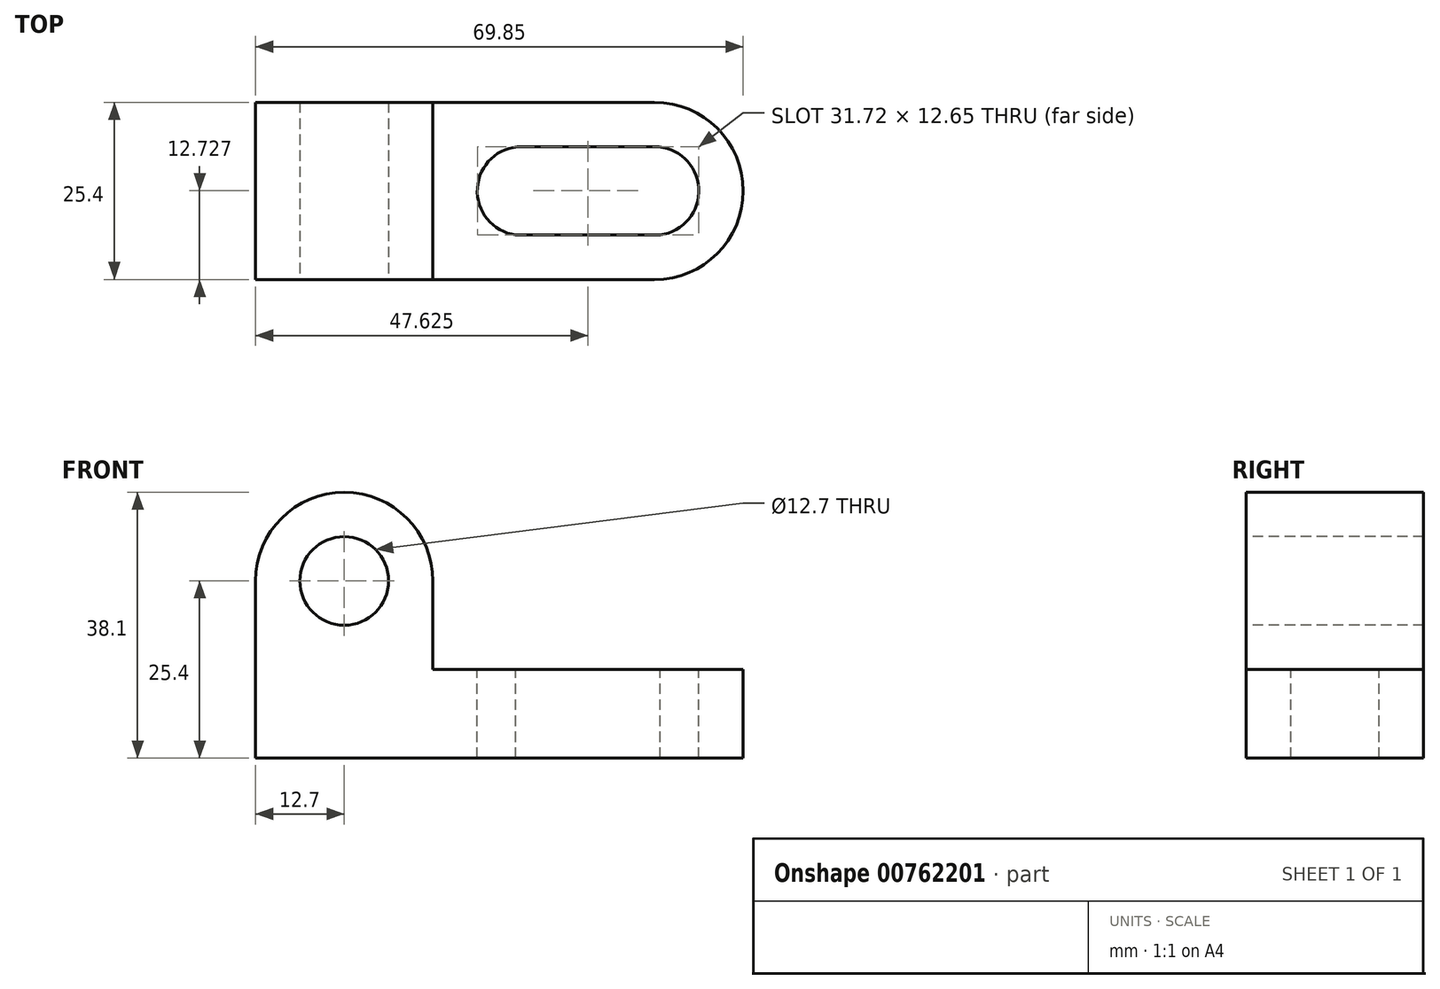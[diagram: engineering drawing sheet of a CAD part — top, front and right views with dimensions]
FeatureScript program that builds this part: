
annotation { "Feature Type Name" : "Feature", "Feature Type Description" : "" }
export const myFeature = defineFeature(function(context is Context, id is Id, definition is map)
    precondition{}
    {
        {
            var Q0;
            Q0=qCreatedBy(makeId("Front.planeOp"),FACE);
            var sketch = newSketch(context, id + "F0", { "sketchPlane" : qUnion([Q0])});
            skLineSegment(sketch, "E0", {"start": v(0, 0) * mm, "end": v(-69.85, 0) * mm});
            skLineSegment(sketch, "E1", {"start": v(-69.85, 0) * mm, "end": v(-69.85, 38.1) * mm});
            skLineSegment(sketch, "E2", {"start": v(-69.85, 38.1) * mm, "end": v(-44.45, 38.1) * mm});
            skLineSegment(sketch, "E3", {"start": v(-44.45, 38.1) * mm, "end": v(-44.45, 12.7) * mm});
            skLineSegment(sketch, "E4", {"start": v(-44.45, 12.7) * mm, "end": v(0, 12.7) * mm});
            skLineSegment(sketch, "E5", {"start": v(0, 12.7) * mm, "end": v(0, 0) * mm});
            skSolve(sketch);
        }
        {
            var Q0;
            Q0=makeQuery(id+"F0.imprint","IMPRINT",FACE,{"disambiguationData":[TD([[makeQuery(id+"F0.imprint","IMPRINT",EDGE,{"derivedFrom":sQuery(id+"F0.wireOp",EDGE,"E0")}),-1.0]])]});
            extrude(context, id + "F1", {"entities" : qUnion([Q0]), "depth" : 25.4 * mm, "offsetDistance" : 25.4 * mm});
        }
        {
            var Q0;
            Q0=makeQuery(id+"F0.imprint","IMPRINT",FACE,{"disambiguationData":[TD([[makeQuery(id+"F0.imprint","IMPRINT",EDGE,{"derivedFrom":sQuery(id+"F0.wireOp",EDGE,"E0")}),-1.0]])]});
            extrude(context, id + "F2", {"entities" : qUnion([Q0]), "operationType" : NewBodyOperationType.ADD, "depth" : 25.4 * mm, "offsetDistance" : 25.4 * mm});
        }
        {
            var Q0;
            Q0=makeQuery(id+"F1.opExtrude","SWEPT_FACE",FACE,{"disambiguationData":[OSD([sQuery(id+"F0.wireOp",EDGE,"E4")])]});
            var sketch = newSketch(context, id + "F3", { "sketchPlane" : qUnion([Q0])});
            skLineSegment(sketch, "E6", {"start": v(-38.1, 0) * mm, "end": v(-38.1, -25.4) * mm});
            skLineSegment(sketch, "E7", {"start": v(-6.35, 0) * mm, "end": v(-6.35, -25.4) * mm});
            skLineSegment(sketch, "E8", {"start": v(-38.1, -6.35) * mm, "end": v(-6.35, -6.35) * mm});
            skLineSegment(sketch, "E9", {"start": v(-38.1, -19) * mm, "end": v(-6.35, -19) * mm});
            skCircle(sketch, "E10", {"center": v(2.1, -12.84) * mm, "radius": 1.17 * mm});
            skLineSegment(sketch, "E11", {"start": v(-31.75, 0) * mm, "end": v(-31.75, -25.4) * mm});
            skLineSegment(sketch, "E12", {"start": v(-12.7, 0) * mm, "end": v(-12.7, -25.4) * mm});
            skCircle(sketch, "E13", {"center": v(-31.75, -12.7) * mm, "radius": 6.35 * mm});
            skCircle(sketch, "E14", {"center": v(-12.7, -12.7) * mm, "radius": 6.35 * mm});
            skSolve(sketch);
        }
        {
            var Q0;
            {var subQ0=sQuery(id+"F3.wireOp",EDGE,"E11");var subQ1=sQuery(id+"F3.wireOp",EDGE,"E9");var subQ2=makeQuery(id+"F3.imprint","INTERSECT",VERTEX,{"derivedFrom":[subQ1,subQ0]});Q0=makeQuery(id+"F3.imprint","IMPRINT",FACE,{"disambiguationData":[TD([[makeQuery(id+"F3.imprint","IMPRINT",EDGE,{"disambiguationData":[TD([[subQ2,-1.0]])],"derivedFrom":subQ1}),1.0]])]});}
            var Q1;
            {var subQ0=sQuery(id+"F3.wireOp",EDGE,"E13");var subQ1=sQuery(id+"F3.wireOp",EDGE,"E9");var subQ2=makeQuery(id+"F3.imprint","INTERSECT",VERTEX,{"disambiguationData":[OD(0.0)],"derivedFrom":[subQ1,subQ0]});Q1=makeQuery(id+"F3.imprint","IMPRINT",FACE,{"disambiguationData":[TD([[makeQuery(id+"F3.imprint","IMPRINT",EDGE,{"disambiguationData":[TD([[subQ2,-1.0]])],"derivedFrom":subQ1}),1.0]])]});}
            var Q2;
            {var subQ0=sQuery(id+"F3.wireOp",EDGE,"E14");var subQ1=sQuery(id+"F3.wireOp",EDGE,"E9");var subQ2=makeQuery(id+"F3.imprint","INTERSECT",VERTEX,{"disambiguationData":[OD(0.0)],"derivedFrom":[subQ1,subQ0]});Q2=makeQuery(id+"F3.imprint","IMPRINT",FACE,{"disambiguationData":[TD([[makeQuery(id+"F3.imprint","IMPRINT",EDGE,{"disambiguationData":[TD([[subQ2,-1.0]])],"derivedFrom":subQ1}),1.0]])]});}
            var Q3;
            {var subQ0=sQuery(id+"F3.wireOp",EDGE,"E13");var subQ5=sQuery(id+"F3.wireOp",EDGE,"E9");var subQ6=makeQuery(id+"F3.imprint","INTERSECT",VERTEX,{"disambiguationData":[OD(1.0)],"derivedFrom":[subQ5,subQ0]});Q3=makeQuery(id+"F3.imprint","IMPRINT",FACE,{"disambiguationData":[TD([[makeQuery(id+"F3.imprint","IMPRINT",EDGE,{"disambiguationData":[TD([[subQ6,-1.0]])],"derivedFrom":subQ5}),1.0]])]});}
            var Q4;
            {var subQ0=sQuery(id+"F3.wireOp",EDGE,"E12");var subQ1=sQuery(id+"F3.wireOp",EDGE,"E9");var subQ2=makeQuery(id+"F3.imprint","INTERSECT",VERTEX,{"derivedFrom":[subQ1,subQ0]});Q4=makeQuery(id+"F3.imprint","IMPRINT",FACE,{"disambiguationData":[TD([[makeQuery(id+"F3.imprint","IMPRINT",EDGE,{"disambiguationData":[TD([[subQ2,-1.0]])],"derivedFrom":subQ1}),1.0]])]});}
            extrude(context, id + "F4", {"entities" : qUnion([Q0, Q1, Q2, Q3, Q4]), "operationType" : NewBodyOperationType.REMOVE, "endBound" : BoundingType.THROUGH_ALL, "oppositeDirection" : true, "depth" : 25.4 * mm, "offsetDistance" : 25.4 * mm});
        }
        {
            var Q0;
            Q0=makeQuery(id+"F1.opExtrude","SWEPT_FACE",FACE,{"disambiguationData":[OSD([sQuery(id+"F0.wireOp",EDGE,"E4")])]});
            var sketch = newSketch(context, id + "F5", { "sketchPlane" : qUnion([Q0])});
            skLineSegment(sketch, "E15", {"start": v(-12.7, 0) * mm, "end": v(-12.7, -25.4) * mm});
            skArc(sketch, "E16", {"start": v(-12.7, -25.4) * mm, "mid": v(0, -12.7) * mm, "end": v(-12.7, 0) * mm});
            skSolve(sketch);
        }
        {
            var Q0;
            {var subQ0=sQuery(id+"F5.wireOp",EDGE,"E16");var subQ1=sQuery(id+"F0.wireOp",EDGE,"E4");var subQ2=makeQuery(id+"F1.opExtrude","CAP_EDGE",EDGE,{"disambiguationData":[OSD([subQ1])],"isStart":false});var subQ3=makeQuery(id+"F5.imprint","INTERSECT",VERTEX,{"derivedFrom":[subQ2,sQuery(id+"F5.wireOp",EDGE,"E15"),subQ0]});Q0=makeQuery(id+"F5.imprint","IMPRINT",FACE,{"disambiguationData":[TD([[makeQuery(id+"F5.imprint","IMPRINT",EDGE,{"disambiguationData":[TD([[subQ3,-1.0]])],"derivedFrom":subQ0}),-1.0]])]});}
            var Q1;
            {var subQ0=sQuery(id+"F5.wireOp",EDGE,"E16");var subQ1=sQuery(id+"F0.wireOp",EDGE,"E4");var subQ2=makeQuery(id+"F1.opExtrude","CAP_EDGE",EDGE,{"disambiguationData":[OSD([subQ1])],"isStart":true});var subQ3=makeQuery(id+"F5.imprint","INTERSECT",VERTEX,{"derivedFrom":[subQ2,sQuery(id+"F5.wireOp",EDGE,"E15"),subQ0]});Q1=makeQuery(id+"F5.imprint","IMPRINT",FACE,{"disambiguationData":[TD([[makeQuery(id+"F5.imprint","IMPRINT",EDGE,{"disambiguationData":[TD([[subQ3,1.0]])],"derivedFrom":subQ0}),-1.0]])]});}
            extrude(context, id + "F6", {"entities" : qUnion([Q0, Q1]), "operationType" : NewBodyOperationType.REMOVE, "endBound" : BoundingType.THROUGH_ALL, "oppositeDirection" : true, "depth" : 25.4 * mm, "offsetDistance" : 25.4 * mm});
        }
        {
            var Q0;
            Q0=makeQuery(id+"F1.opExtrude","CAP_FACE",FACE,{"disambiguationData":[OSD([sQuery(id+"F0.wireOp",EDGE,"E0"),sQuery(id+"F0.wireOp",EDGE,"E1"),sQuery(id+"F0.wireOp",EDGE,"E2"),sQuery(id+"F0.wireOp",EDGE,"E3"),sQuery(id+"F0.wireOp",EDGE,"E4"),sQuery(id+"F0.wireOp",EDGE,"E5")])],"isStart":false});
            var sketch = newSketch(context, id + "F7", { "sketchPlane" : qUnion([Q0])});
            skLineSegment(sketch, "E17", {"start": v(-44.45, 12.7) * mm, "end": v(-69.85, 12.7) * mm});
            skLineSegment(sketch, "E18", {"start": v(-69.85, 25.4) * mm, "end": v(-44.45, 25.4) * mm});
            skCircle(sketch, "E19", {"center": v(-57.15, 25.4) * mm, "radius": 6.35 * mm});
            skArc(sketch, "E20", {"start": v(-44.45, 25.4) * mm, "mid": v(-57.15, 38.1) * mm, "end": v(-69.85, 25.4) * mm});
            skSolve(sketch);
        }
        {
            var Q0;
            {var subQ0=sQuery(id+"F7.wireOp",EDGE,"E19");var subQ1=sQuery(id+"F7.wireOp",EDGE,"E18");var subQ2=makeQuery(id+"F7.imprint","INTERSECT",VERTEX,{"disambiguationData":[OD(0.0)],"derivedFrom":[subQ1,subQ0]});Q0=makeQuery(id+"F7.imprint","IMPRINT",FACE,{"disambiguationData":[TD([[makeQuery(id+"F7.imprint","IMPRINT",EDGE,{"disambiguationData":[TD([[subQ2,-1.0]])],"derivedFrom":subQ1}),-1.0]])]});}
            var Q1;
            {var subQ0=sQuery(id+"F7.wireOp",EDGE,"E19");var subQ1=sQuery(id+"F7.wireOp",EDGE,"E18");var subQ2=makeQuery(id+"F7.imprint","INTERSECT",VERTEX,{"disambiguationData":[OD(0.0)],"derivedFrom":[subQ1,subQ0]});Q1=makeQuery(id+"F7.imprint","IMPRINT",FACE,{"disambiguationData":[TD([[makeQuery(id+"F7.imprint","IMPRINT",EDGE,{"disambiguationData":[TD([[subQ2,-1.0]])],"derivedFrom":subQ1}),1.0]])]});}
            var Q2;
            {var subQ1=makeQuery(id+"F1.opExtrude","CAP_EDGE",EDGE,{"disambiguationData":[OSD([sQuery(id+"F0.wireOp",EDGE,"E1")])],"isStart":false});var subQ3=makeQuery(id+"F1.opExtrude","CAP_EDGE",EDGE,{"disambiguationData":[OSD([sQuery(id+"F0.wireOp",EDGE,"E2")])],"isStart":false});var subQ5=makeQuery(id+"F7.imprint","INTERSECT",VERTEX,{"derivedFrom":[subQ1,subQ3]});Q2=makeQuery(id+"F7.imprint","IMPRINT",FACE,{"disambiguationData":[TD([[makeQuery(id+"F7.imprint","IMPRINT",EDGE,{"disambiguationData":[TD([[subQ5,-1.0]])],"derivedFrom":subQ3}),-1.0]])]});}
            var Q3;
            {var subQ1=makeQuery(id+"F1.opExtrude","CAP_EDGE",EDGE,{"disambiguationData":[OSD([sQuery(id+"F0.wireOp",EDGE,"E3")])],"isStart":false});var subQ3=makeQuery(id+"F1.opExtrude","CAP_EDGE",EDGE,{"disambiguationData":[OSD([sQuery(id+"F0.wireOp",EDGE,"E2")])],"isStart":false});var subQ5=makeQuery(id+"F7.imprint","INTERSECT",VERTEX,{"derivedFrom":[subQ3,subQ1]});Q3=makeQuery(id+"F7.imprint","IMPRINT",FACE,{"disambiguationData":[TD([[makeQuery(id+"F7.imprint","IMPRINT",EDGE,{"disambiguationData":[TD([[subQ5,1.0]])],"derivedFrom":subQ3}),-1.0]])]});}
            extrude(context, id + "F8", {"entities" : qUnion([Q0, Q1, Q2, Q3]), "operationType" : NewBodyOperationType.REMOVE, "endBound" : BoundingType.THROUGH_ALL, "oppositeDirection" : true, "depth" : 25.4 * mm, "offsetDistance" : 25.4 * mm});
        }
    });
